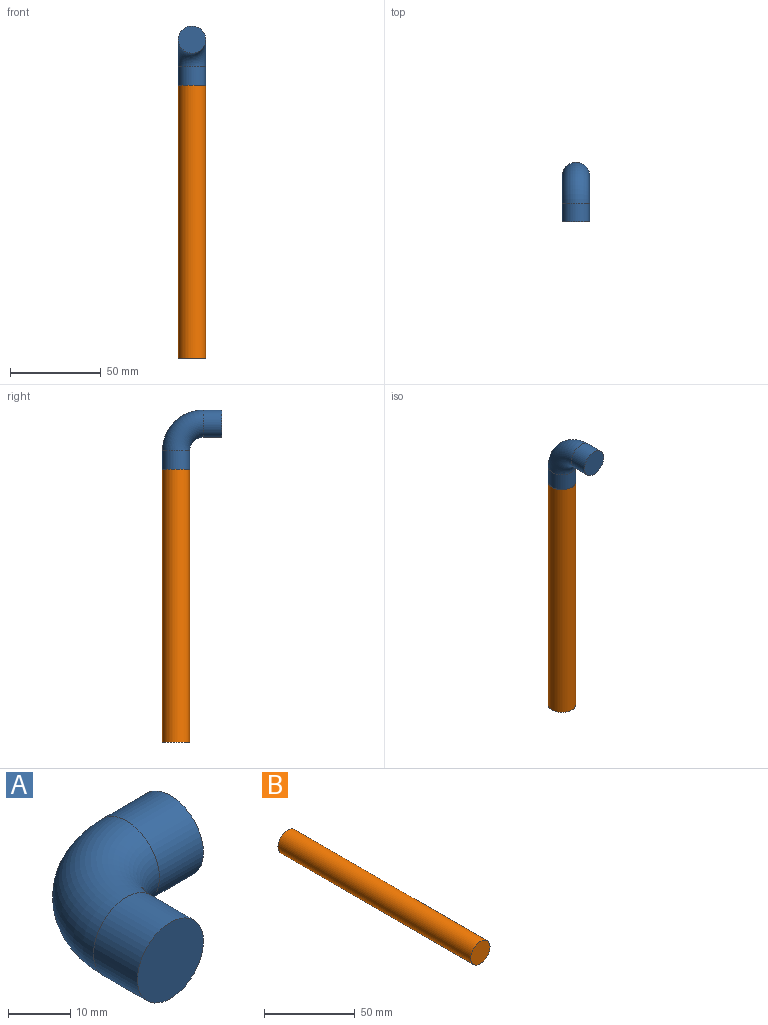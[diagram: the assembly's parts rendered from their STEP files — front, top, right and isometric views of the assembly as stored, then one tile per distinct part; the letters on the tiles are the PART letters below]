
ASSEMBLY  parts=2 mates=1
PART A: 5 faces, bbox 34.4x34.4x15 mm
  f0: plane 15x15mm, normal (0,-1,0), area 176.7mm2, adj f2
  f1: plane 15x15mm, normal (1,0,0), area 176.7mm2, adj f4
  f2: cylinder r=7.5mm len=15mm, axis (0,1,0), area 471.2mm2, adj f0,f3
  f3: torus R=15mm, axis (0,0,-1), area 1110.3mm2, adj f2,f4
  f4: cylinder r=7.5mm len=15mm, axis (1,0,0), area 471.2mm2, adj f1,f3
PART B: 3 faces, bbox 15x150x15 mm
  f0: cylinder r=7.5mm len=150mm, axis (0,1,0), area 7068.6mm2, adj f1,f2
  f1: plane 15x15mm, normal (0,-1,0), area 176.7mm2, adj f0
  f2: plane 15x15mm, normal (0,1,0), area 176.7mm2, adj f0
PLACE A rot(axis=(0,1,0),90deg) t=(13342.77,3174.64,-1325)mm
PLACE B rot(axis=(1,0,0),90deg) t=(13404.2,3236.23,-1350)mm
MATE fastened A.f4 <-> B.f0  axis (0,0,-1) through (13342.77,3199.64,-1350)mm
